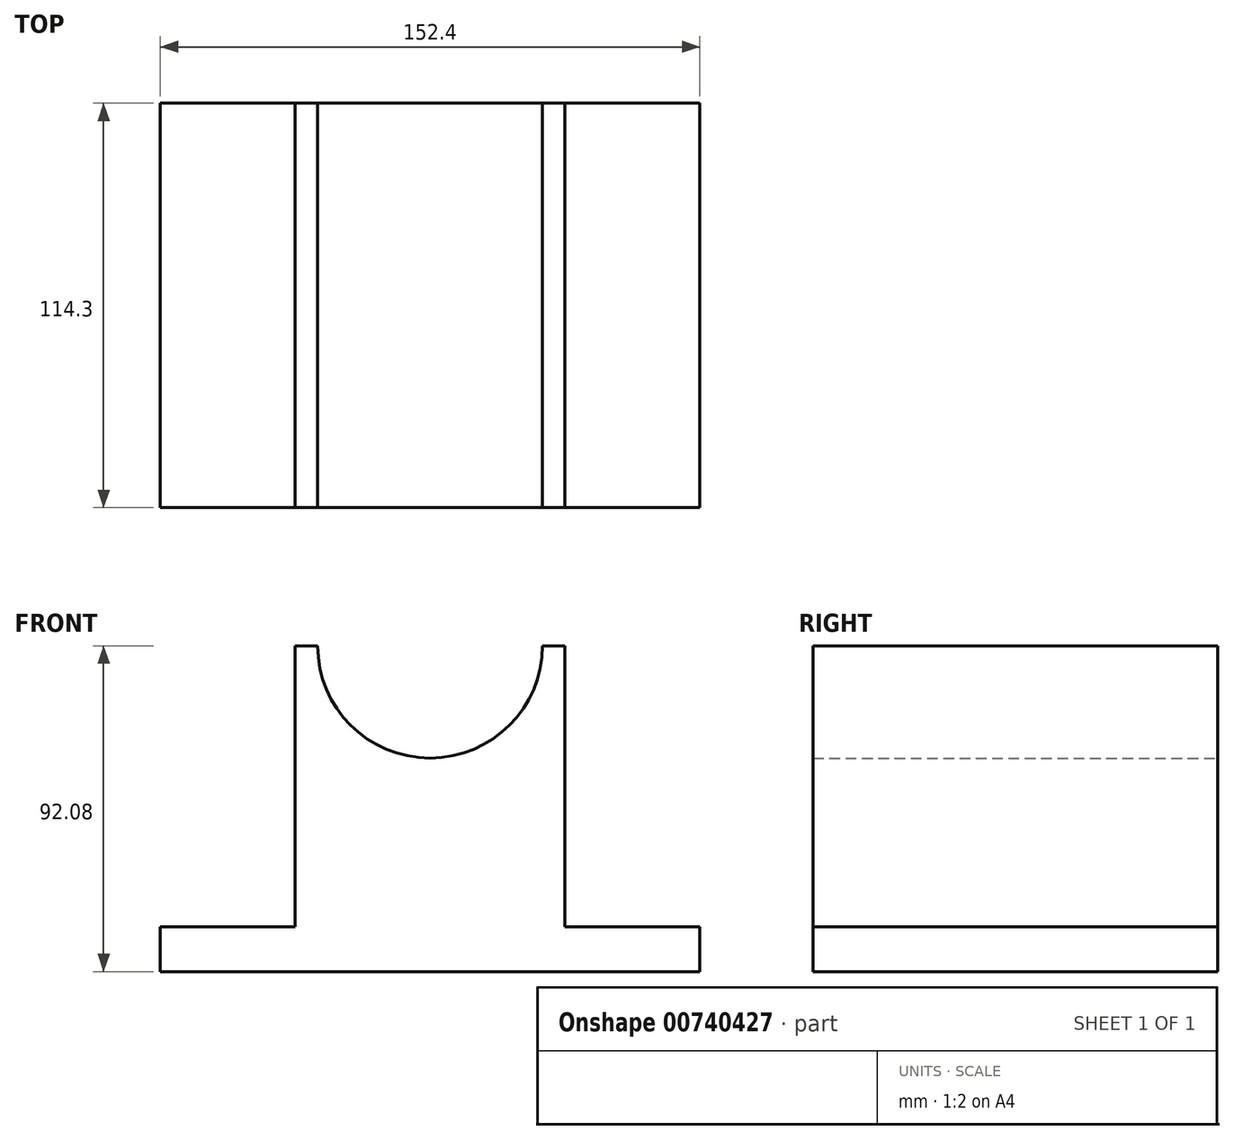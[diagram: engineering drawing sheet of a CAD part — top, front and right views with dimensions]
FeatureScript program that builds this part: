
annotation { "Feature Type Name" : "Feature", "Feature Type Description" : "" }
export const myFeature = defineFeature(function(context is Context, id is Id, definition is map)
    precondition{}
    {
        {
            var Q0;
            Q0=qCreatedBy(makeId("Front.planeOp"),FACE);
            var sketch = newSketch(context, id + "F0", { "sketchPlane" : qUnion([Q0])});
            skLineSegment(sketch, "E0", {"start": v(-97.58, -65.85) * mm, "end": v(-21.38, -65.85) * mm});
            skLineSegment(sketch, "E1", {"start": v(-97.58, -65.85) * mm, "end": v(-97.58, -53.15) * mm});
            skLineSegment(sketch, "E2", {"start": v(-97.58, -53.15) * mm, "end": v(-59.48, -53.15) * mm});
            skLineSegment(sketch, "E3", {"start": v(-59.48, -53.15) * mm, "end": v(-59.48, 26.23) * mm});
            skLineSegment(sketch, "E4", {"start": v(-59.48, 26.23) * mm, "end": v(-53.13, 26.23) * mm});
            skLineSegment(sketch, "E5.MirrorCS", {"start": v(16.72, 26.23) * mm, "end": v(10.37, 26.23) * mm});
            skLineSegment(sketch, "E6.MirrorCS", {"start": v(16.72, -53.15) * mm, "end": v(16.72, 26.23) * mm});
            skLineSegment(sketch, "E7.MirrorCS", {"start": v(54.82, -53.15) * mm, "end": v(16.72, -53.15) * mm});
            skLineSegment(sketch, "E8.MirrorCS", {"start": v(54.82, -65.85) * mm, "end": v(54.82, -53.15) * mm});
            skLineSegment(sketch, "E9.MirrorCS", {"start": v(54.82, -65.85) * mm, "end": v(-21.38, -65.85) * mm});
            skArc(sketch, "E10", {"start": v(10.37, 26.23) * mm, "mid": v(-21.38, -5.52) * mm, "end": v(-53.13, 26.23) * mm});
            skSolve(sketch);
        }
        {
            var Q0;
            Q0=qSketchRegion(id+"F0",true);
            extrude(context, id + "F1", {"entities" : qUnion([Q0]), "depth" : 114.3 * mm});
        }
    });
